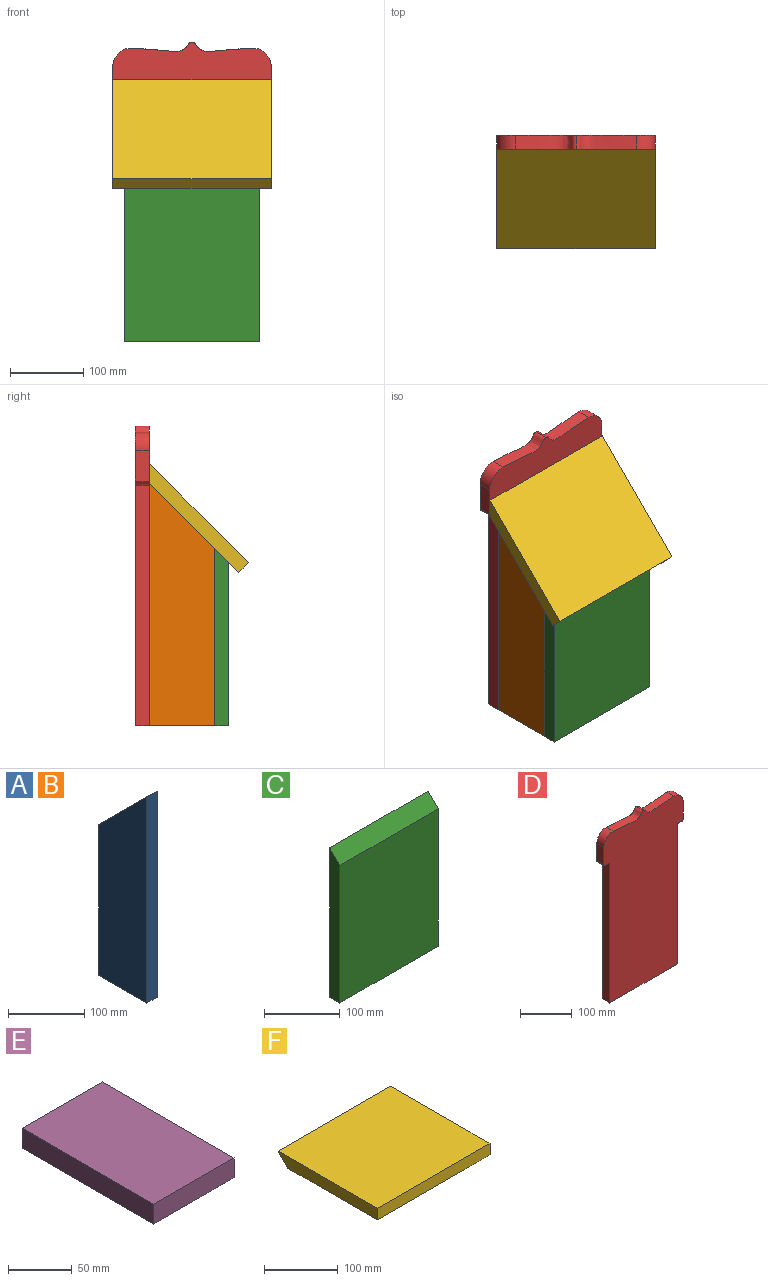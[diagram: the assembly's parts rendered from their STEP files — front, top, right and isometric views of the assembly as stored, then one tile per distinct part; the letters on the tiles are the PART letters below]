
ASSEMBLY  parts=6 mates=5
PART A: 6 faces, bbox 19.1x88.9x330.2 mm
  f0: plane 330.2x19.05mm, normal (0,-1,0), area 6290.3mm2, adj f1,f3,f4,f5
  f1: plane 88.9x19.05mm, normal (0,0,-1), area 1693.5mm2, adj f0,f2,f4,f5
  f2: plane 241.3x19.05mm, normal (0,1,0), area 4596.8mm2, adj f1,f3,f4,f5
  f3: plane 88.9x88.9mm, normal (0,0.71,0.71), area 2395mm2, adj f0,f2,f4,f5
  f4: plane 330.2x88.9mm, normal (1,0,0), area 25403.2mm2, adj f0,f1,f2,f3
  f5: plane 330.2x88.9mm, normal (-1,0,0), area 25403.2mm2, adj f0,f1,f2,f3
PART B: same geometry as A
PART C: 6 faces, bbox 184.2x19.1x241.3 mm
  f0: plane 241.3x19.05mm, normal (1,0,0), area 4415.3mm2, adj f2,f3,f4,f5
  f1: plane 241.3x19.05mm, normal (-1,0,0), area 4415.3mm2, adj f2,f3,f4,f5
  f2: plane 184.15x19.05mm, normal (0,0,-1), area 3508.1mm2, adj f0,f1,f3,f4
  f3: plane 222.25x184.15mm, normal (0,-1,0), area 40927.3mm2, adj f0,f1,f2,f5
  f4: plane 241.3x184.15mm, normal (0,1,0), area 44435.4mm2, adj f0,f1,f2,f5
  f5: plane 184.15x19.05mm, normal (0,-0.71,0.71), area 4961.1mm2, adj f0,f1,f3,f4
PART D: 17 faces, bbox 215.9x19.1x408 mm
  f0: plane 327.03x19.05mm, normal (1,0,0), area 6229.8mm2, adj f2,f3,f4,f15
  f1: plane 327.03x19.05mm, normal (-1,0,0), area 6229.8mm2, adj f2,f3,f4,f16
  f2: plane 184.15x19.05mm, normal (0,0,-1), area 3508.1mm2, adj f0,f1,f3,f4
  f3: plane 408x215.9mm, normal (0,-1,0), area 75355.3mm2, adj f0,f1,f2,f5,f6,f7,f8,f9
  f4: plane 408x215.9mm, normal (0,1,0), area 75355.3mm2, adj f0,f1,f2,f5,f6,f7,f8,f9
  f5: plane 19.05x9.53mm, normal (0,0,-1), area 181.5mm2, adj f3,f4,f13,f15
  f6: plane 41.28x19.05mm, normal (1,0,0), area 786.3mm2, adj f3,f4,f7,f13
  f7: cylinder r=25.4mm len=25.4mm, axis (0,-1,0), area 760.1mm2, adj f3,f4,f6,f8
  f8: extruded ~82.55x19.05mm, area 1664.1mm2, adj f3,f4,f7,f9
  f9: extruded ~82.55x19.05mm, area 1664.1mm2, adj f3,f4,f8,f11
  f10: plane 19.05x9.53mm, normal (0,0,-1), area 181.5mm2, adj f3,f4,f14,f16
  f11: cylinder r=25.4mm len=25.4mm, axis (0,-1,0), area 760.1mm2, adj f3,f4,f9,f12
  f12: plane 41.28x19.05mm, normal (-1,0,0), area 786.3mm2, adj f3,f4,f11,f14
  f13: cylinder r=3.17mm len=19.05mm, axis (0,-1,0), area 95mm2, adj f3,f4,f5,f6
  f14: cylinder r=3.17mm len=19.05mm, axis (0,-1,0), area 95mm2, adj f3,f4,f10,f12
  f15: cylinder r=3.17mm len=19.05mm, axis (0,1,0), area 95mm2, adj f0,f3,f4,f5
  f16: cylinder r=3.17mm len=19.05mm, axis (0,-1,0), area 95mm2, adj f1,f3,f4,f10
PART E: 6 faces, bbox 88.9x146.1x19.1 mm
  f0: plane 146.05x19.05mm, normal (1,0,0), area 2782.3mm2, adj f1,f3,f4,f5
  f1: plane 88.9x19.05mm, normal (0,1,0), area 1693.5mm2, adj f0,f2,f4,f5
  f2: plane 146.05x19.05mm, normal (-1,0,0), area 2782.3mm2, adj f1,f3,f4,f5
  f3: plane 88.9x19.05mm, normal (0,-1,0), area 1693.5mm2, adj f0,f2,f4,f5
  f4: plane 146.05x88.9mm, normal (0,0,1), area 12983.8mm2, adj f0,f1,f2,f3
  f5: plane 146.05x88.9mm, normal (0,0,-1), area 12983.8mm2, adj f0,f1,f2,f3
PART F: 6 faces, bbox 215.9x190.5x19.1 mm
  f0: plane 190.5x19.05mm, normal (1,0,0), area 3447.6mm2, adj f2,f3,f4,f5
  f1: plane 190.5x19.05mm, normal (-1,0,0), area 3447.6mm2, adj f2,f3,f4,f5
  f2: plane 215.9x19.05mm, normal (0,-1,0), area 4112.9mm2, adj f0,f1,f3,f4
  f3: plane 215.9x190.5mm, normal (0,0,1), area 41129mm2, adj f0,f1,f2,f5
  f4: plane 215.9x171.45mm, normal (0,0,-1), area 37016.1mm2, adj f0,f1,f2,f5
  f5: plane 215.9x19.05mm, normal (0,0.71,-0.71), area 5816.5mm2, adj f0,f1,f3,f4
PLACE A rot(axis=(0,0,1),180deg) t=(92.07,44.45,44.45)mm
PLACE B rot(axis=(0,0,1),180deg) t=(-73.03,44.45,44.45)mm
PLACE C at identity fixed
PLACE D t=(0,107.95,44.45)mm
PLACE E rot(axis=(0,0,-1),90deg) t=(0,44.45,-120.65)mm
PLACE F rot(axis=(1,0,0),45deg) t=(0,34.83,155.48)mm
MATE fastened F.f4 <-> C.f5  axis (0,0.71,-0.71) through (107.95,-32.52,88.13)mm
MATE fastened A.f2 <-> C.f4  axis (0,-1,0) through (92.07,0,-120.65)mm
MATE fastened B.f2 <-> C.f4  axis (0,-1,0) through (-92.08,0,-120.65)mm
MATE fastened D.f3 <-> A.f0  axis (0,-1,0) through (92.07,88.9,-120.65)mm
MATE fastened E.f3 <-> B.f5  axis (-1,0,0) through (-73.03,0,-120.65)mm
